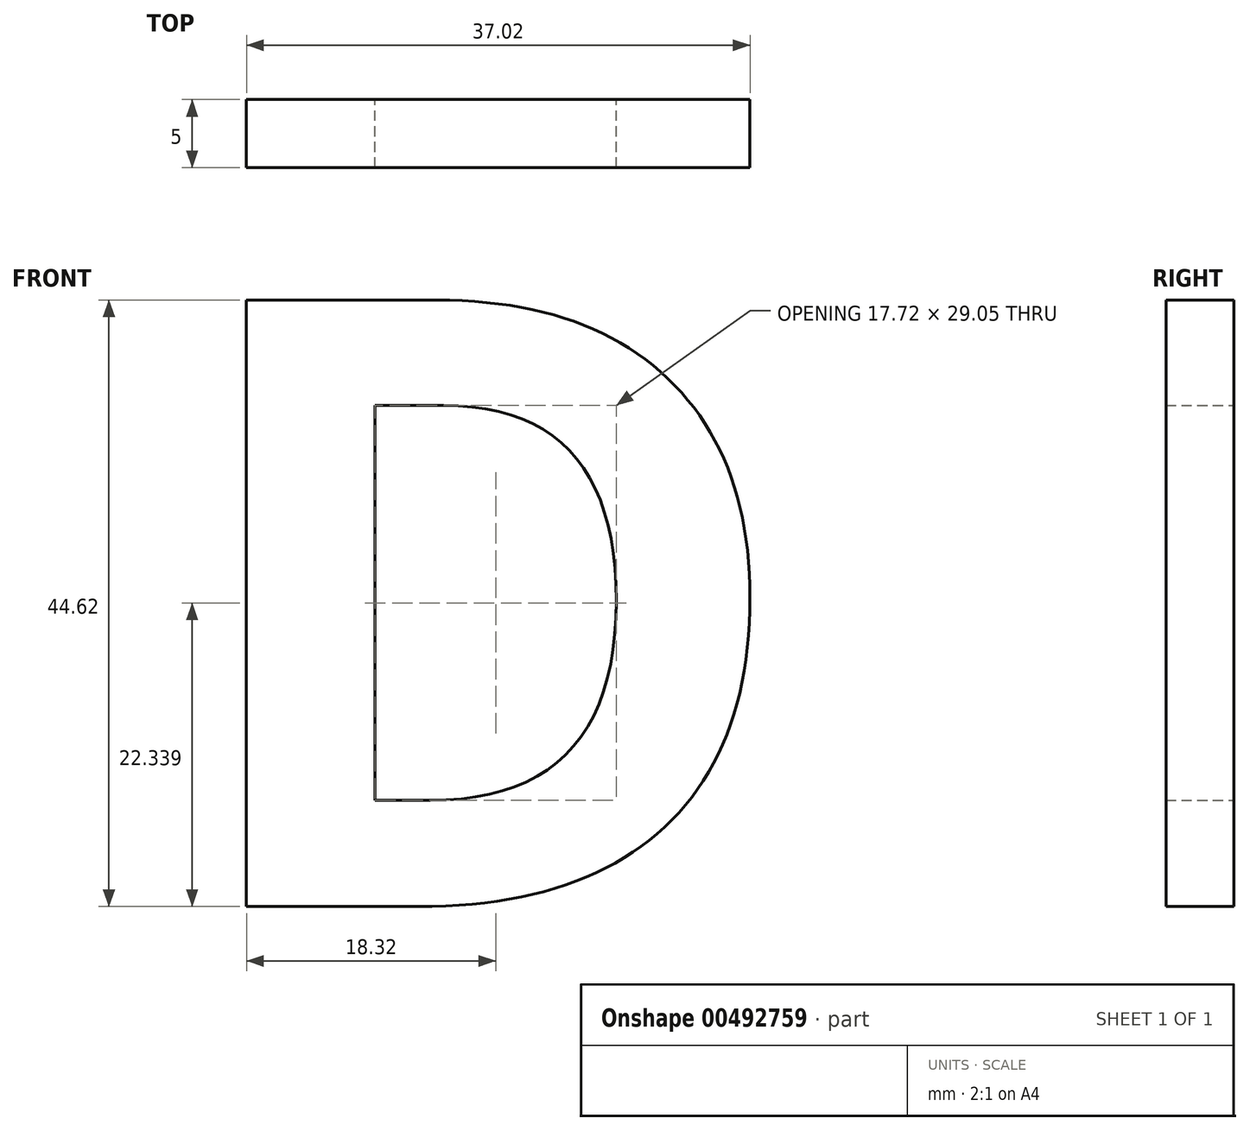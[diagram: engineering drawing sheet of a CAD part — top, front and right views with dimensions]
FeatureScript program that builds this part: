
annotation { "Feature Type Name" : "Feature", "Feature Type Description" : "" }
export const myFeature = defineFeature(function(context is Context, id is Id, definition is map)
    precondition{}
    {
        {
            var Q0;
            Q0=qCreatedBy(makeId("Front.planeOp"),FACE);
            var sketch = newSketch(context, id + "F0", { "sketchPlane" : qUnion([Q0])});
            skText(sketch, "E0", { "text": "D", "fontName": "OpenSans-Bold.ttf"});
            const initialGuessF0  = {"E0": [-0.07001, 0.01496, 1, 0, 0.045]};
            skSetInitialGuess(sketch, initialGuessF0);
            skSolve(sketch);
        }
        {
            var Q0;
            Q0=makeQuery(id+"F0.imprint","IMPRINT",FACE,{"disambiguationData":[TD([[makeQuery(id+"F0.imprint","IMPRINT",EDGE,{"derivedFrom":sQuery(id+"F0.wireOp",EDGE,"E0.sketch_text.stroke-0")}),-1.0]])]});
            extrude(context, id + "F1", {"entities" : qUnion([Q0]), "depth" : 5 * mm});
        }
    });
